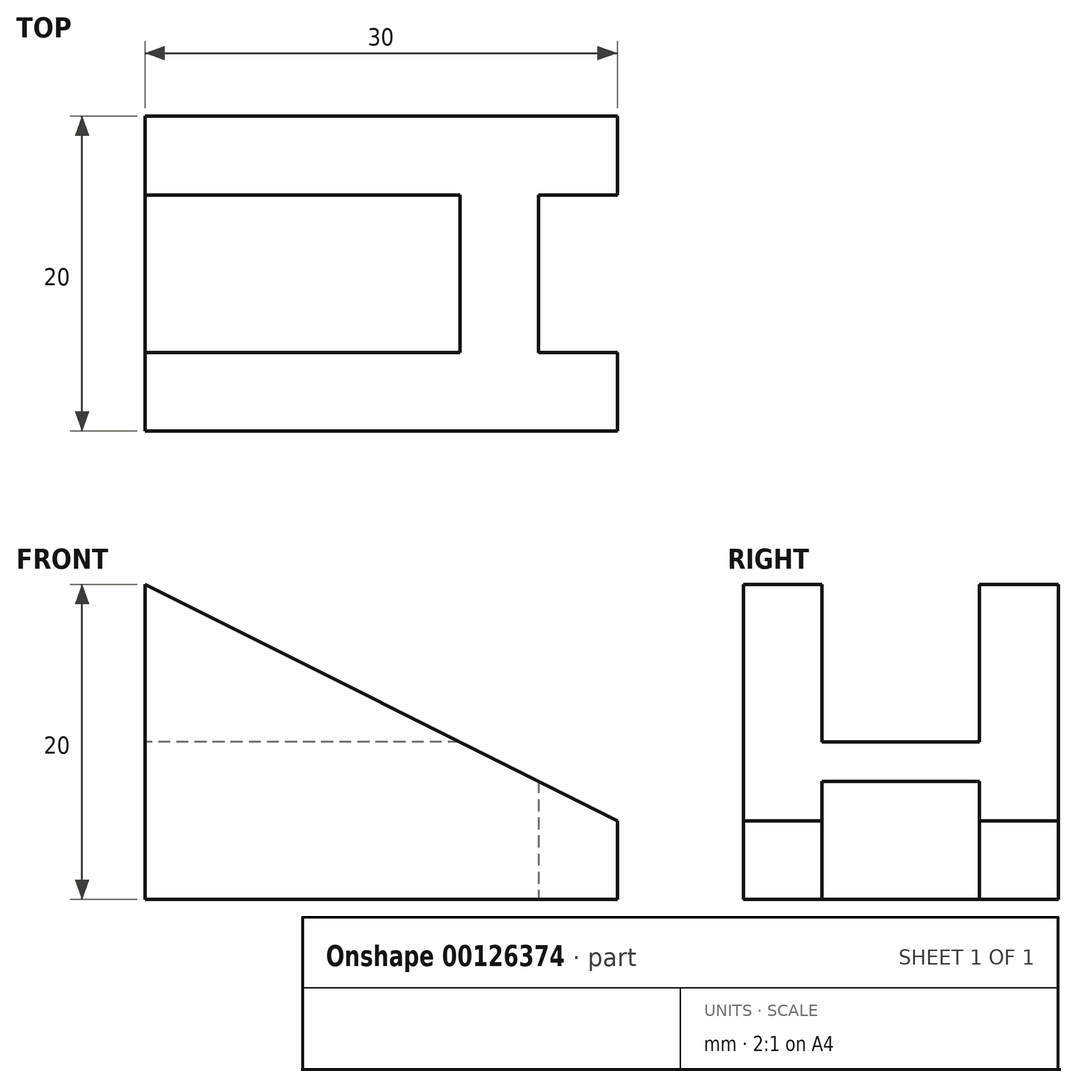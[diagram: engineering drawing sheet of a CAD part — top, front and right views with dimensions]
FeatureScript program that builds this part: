
annotation { "Feature Type Name" : "Feature", "Feature Type Description" : "" }
export const myFeature = defineFeature(function(context is Context, id is Id, definition is map)
    precondition{}
    {
        {
            var Q0;
            Q0=qCreatedBy(makeId("Front.planeOp"),FACE);
            var sketch = newSketch(context, id + "F0", { "sketchPlane" : qUnion([Q0])});
            skLineSegment(sketch, "E0", {"start": v(0, 0) * mm, "end": v(0, 20) * mm});
            skLineSegment(sketch, "E1", {"start": v(0, 20) * mm, "end": v(30, 5) * mm});
            skLineSegment(sketch, "E2", {"start": v(30, 5) * mm, "end": v(30, 0) * mm});
            skLineSegment(sketch, "E3", {"start": v(30, 0) * mm, "end": v(0, 0) * mm});
            skSolve(sketch);
        }
        {
            var Q0;
            Q0 = qSketchRegion(id + "F0", true);
            extrude(context, id + "F1", {"entities" : qUnion([Q0]), "depth" : 20 * mm});
        }
        {
            var Q0;
            Q0=makeQuery(id+"F1.opExtrude","SWEPT_FACE",FACE,{"disambiguationData":[OSD([sQuery(id+"F0.wireOp",EDGE,"E3")])]});
            var sketch = newSketch(context, id + "F2", { "sketchPlane" : qUnion([Q0])});
            skLineSegment(sketch, "E4.bottom", {"start": v(30, 15) * mm, "end": v(25, 15) * mm});
            skLineSegment(sketch, "E4.top", {"start": v(30, 5) * mm, "end": v(25, 5) * mm});
            skLineSegment(sketch, "E4.left", {"start": v(30, 15) * mm, "end": v(30, 5) * mm});
            skLineSegment(sketch, "E4.right", {"start": v(25, 15) * mm, "end": v(25, 5) * mm});
            skSolve(sketch);
        }
        {
            var Q0;
            Q0 = qSketchRegion(id + "F2", true);
            extrude(context, id + "F3", {"entities" : qUnion([Q0]), "operationType" : NewBodyOperationType.REMOVE, "endBound" : BoundingType.THROUGH_ALL, "oppositeDirection" : true, "depth" : 25 * mm});
        }
        {
            var Q0;
            Q0=makeQuery(id+"F1.opExtrude","SWEPT_FACE",FACE,{"disambiguationData":[OSD([sQuery(id+"F0.wireOp",EDGE,"E0")])]});
            var sketch = newSketch(context, id + "F4", { "sketchPlane" : qUnion([Q0])});
            skLineSegment(sketch, "E5.bottom", {"start": v(5, 20) * mm, "end": v(15, 20) * mm});
            skLineSegment(sketch, "E5.top", {"start": v(5, 10) * mm, "end": v(15, 10) * mm});
            skLineSegment(sketch, "E5.left", {"start": v(5, 20) * mm, "end": v(5, 10) * mm});
            skLineSegment(sketch, "E5.right", {"start": v(15, 20) * mm, "end": v(15, 10) * mm});
            skSolve(sketch);
        }
        {
            var Q0;
            Q0 = qSketchRegion(id + "F4", true);
            extrude(context, id + "F5", {"entities" : qUnion([Q0]), "operationType" : NewBodyOperationType.REMOVE, "endBound" : BoundingType.THROUGH_ALL, "oppositeDirection" : true, "depth" : 25 * mm});
        }
    });
